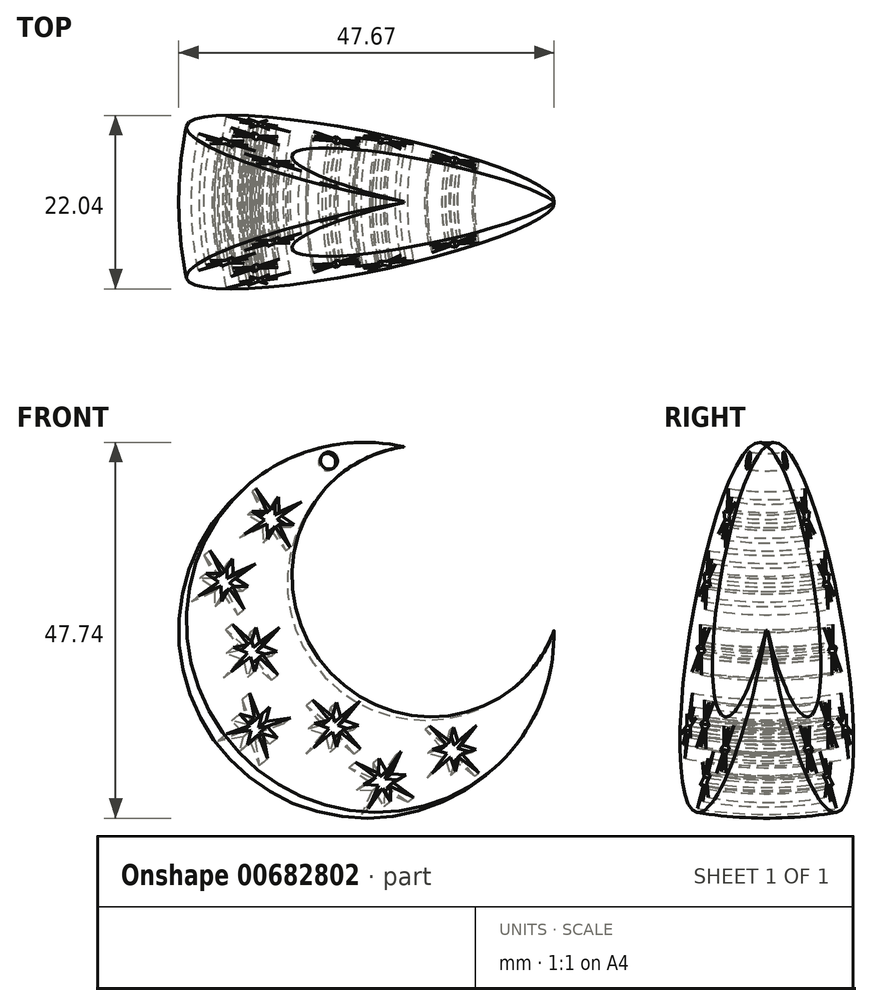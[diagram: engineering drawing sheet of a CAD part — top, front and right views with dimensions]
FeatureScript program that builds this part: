
annotation { "Feature Type Name" : "Feature", "Feature Type Description" : "" }
export const myFeature = defineFeature(function(context is Context, id is Id, definition is map)
    precondition{}
    {
        {
            var Q0;
            Q0=qCreatedBy(makeId("Front.planeOp"),FACE);
            var sketch = newSketch(context, id + "F0", { "sketchPlane" : qUnion([Q0])});
            skArc(sketch, "E0", {"start": v(24.25, 23.35) * mm, "mid": v(1.03, -15.08) * mm, "end": v(43.32, 0) * mm});
            skArc(sketch, "E1", {"start": v(24.25, 23.35) * mm, "mid": v(13.4, -4.97) * mm, "end": v(43.32, 0) * mm});
            skSolve(sketch);
        }
        {
            var Q0;
            Q0=qCreatedBy(makeId("Front.planeOp"),FACE);
            var sketch = newSketch(context, id + "F1", { "sketchPlane" : qUnion([Q0])});
            skLineSegment(sketch, "E2", {"start": v(24.45, 23.46) * mm, "end": v(43.82, 0) * mm});
            skSolve(sketch);
        }
        {
            var Q0;
            Q0 = qSketchRegion(id + "F0", true);
            var Q1;
            Q1 = qConstructionFilter(qBodyType(qCreatedBy(id + "F0" ,EDGE), BodyType.WIRE), ConstructionObject.NO);
            var Q2;
            Q2=sQuery(id+"F1.wireOp",EDGE,"E2");
            revolve(context, id + "F2", {"entities" : qUnion([Q0]), "surfaceEntities" : qUnion([Q1]), "axis" : qUnion([Q2]), "revolveType" : RevolveType.SYMMETRIC, "angle" : 30 * degree});
        }
        {
            var Q0;
            Q0=makeQuery(id+"F2.opRevolve","CAP_FACE",FACE,{"disambiguationData":[OSD([sQuery(id+"F0.wireOp",EDGE,"E0"),sQuery(id+"F0.wireOp",EDGE,"E1")])],"isStart":true});
            var sketch = newSketch(context, id + "F3", { "sketchPlane" : qUnion([Q0])});
            skLineSegment(sketch, "E3", {"start": v(3.8, 17) * mm, "end": v(5.2, 14.07) * mm});
            skLineSegment(sketch, "E4", {"start": v(5.75, 14.37) * mm, "end": v(3.8, 17) * mm});
            skLineSegment(sketch, "E5", {"start": v(8.21, 9.52) * mm, "end": v(6.8, 12.45) * mm});
            skLineSegment(sketch, "E6", {"start": v(6.27, 12.15) * mm, "end": v(8.21, 9.52) * mm});
            skLineSegment(sketch, "E7", {"start": v(9.71, 15.47) * mm, "end": v(6.8, 14.08) * mm});
            skLineSegment(sketch, "E8", {"start": v(7.09, 13.53) * mm, "end": v(9.71, 15.47) * mm});
            skLineSegment(sketch, "E9", {"start": v(2.3, 11.04) * mm, "end": v(5.23, 12.43) * mm});
            skLineSegment(sketch, "E10", {"start": v(4.93, 13) * mm, "end": v(2.3, 11.04) * mm});
            skLineSegment(sketch, "E11", {"start": v(6.75, 16.01) * mm, "end": v(5.75, 14.37) * mm});
            skLineSegment(sketch, "E12", {"start": v(6.8, 14.08) * mm, "end": v(6.75, 16.01) * mm});
            skLineSegment(sketch, "E13", {"start": v(8.74, 12.5) * mm, "end": v(7.09, 13.53) * mm});
            skLineSegment(sketch, "E14", {"start": v(6.8, 12.45) * mm, "end": v(8.74, 12.5) * mm});
            skLineSegment(sketch, "E15", {"start": v(5.28, 10.5) * mm, "end": v(6.27, 12.15) * mm});
            skLineSegment(sketch, "E16", {"start": v(5.23, 12.43) * mm, "end": v(5.28, 10.5) * mm});
            skLineSegment(sketch, "E17", {"start": v(3.28, 14.02) * mm, "end": v(4.93, 13) * mm});
            skLineSegment(sketch, "E18", {"start": v(5.2, 14.07) * mm, "end": v(3.28, 14.02) * mm});
            skLineSegment(sketch, "E19", {"start": v(-2.16, 8.8) * mm, "end": v(-0.75, 5.86) * mm});
            skLineSegment(sketch, "E20", {"start": v(-0.21, 6.17) * mm, "end": v(-2.16, 8.8) * mm});
            skLineSegment(sketch, "E21", {"start": v(2.25, 1.32) * mm, "end": v(0.85, 4.25) * mm});
            skLineSegment(sketch, "E22", {"start": v(0.3, 3.95) * mm, "end": v(2.25, 1.32) * mm});
            skLineSegment(sketch, "E23", {"start": v(3.75, 7.27) * mm, "end": v(0.83, 5.88) * mm});
            skLineSegment(sketch, "E24", {"start": v(1.13, 5.32) * mm, "end": v(3.75, 7.27) * mm});
            skLineSegment(sketch, "E25", {"start": v(-3.66, 2.84) * mm, "end": v(-0.74, 4.23) * mm});
            skLineSegment(sketch, "E26", {"start": v(-1.03, 4.79) * mm, "end": v(-3.66, 2.84) * mm});
            skLineSegment(sketch, "E27", {"start": v(0.78, 7.81) * mm, "end": v(-0.21, 6.17) * mm});
            skLineSegment(sketch, "E28", {"start": v(0.83, 5.88) * mm, "end": v(0.78, 7.81) * mm});
            skLineSegment(sketch, "E29", {"start": v(2.78, 4.3) * mm, "end": v(1.13, 5.32) * mm});
            skLineSegment(sketch, "E30", {"start": v(0.85, 4.25) * mm, "end": v(2.78, 4.3) * mm});
            skLineSegment(sketch, "E31", {"start": v(-0.68, 2.3) * mm, "end": v(0.3, 3.95) * mm});
            skLineSegment(sketch, "E32", {"start": v(-0.74, 4.23) * mm, "end": v(-0.68, 2.3) * mm});
            skLineSegment(sketch, "E33", {"start": v(-2.69, 5.82) * mm, "end": v(-1.03, 4.79) * mm});
            skLineSegment(sketch, "E34", {"start": v(-0.75, 5.86) * mm, "end": v(-2.69, 5.82) * mm});
            skLineSegment(sketch, "E35", {"start": v(0.75, -0.62) * mm, "end": v(2.75, -3.17) * mm});
            skLineSegment(sketch, "E36", {"start": v(3.22, -2.76) * mm, "end": v(0.75, -0.62) * mm});
            skLineSegment(sketch, "E37", {"start": v(6.67, -6.95) * mm, "end": v(4.67, -4.4) * mm});
            skLineSegment(sketch, "E38", {"start": v(4.2, -4.81) * mm, "end": v(6.67, -6.95) * mm});
            skLineSegment(sketch, "E39", {"start": v(6.84, -0.82) * mm, "end": v(4.3, -2.8) * mm});
            skLineSegment(sketch, "E40", {"start": v(4.7, -3.29) * mm, "end": v(6.84, -0.82) * mm});
            skLineSegment(sketch, "E41", {"start": v(0.58, -6.75) * mm, "end": v(3.13, -4.76) * mm});
            skLineSegment(sketch, "E42", {"start": v(2.72, -4.28) * mm, "end": v(0.58, -6.75) * mm});
            skLineSegment(sketch, "E43", {"start": v(3.83, -0.93) * mm, "end": v(3.22, -2.76) * mm});
            skLineSegment(sketch, "E44", {"start": v(4.3, -2.8) * mm, "end": v(3.83, -0.93) * mm});
            skLineSegment(sketch, "E45", {"start": v(6.54, -3.93) * mm, "end": v(4.7, -3.29) * mm});
            skLineSegment(sketch, "E46", {"start": v(4.67, -4.4) * mm, "end": v(6.54, -3.93) * mm});
            skLineSegment(sketch, "E47", {"start": v(3.6, -6.63) * mm, "end": v(4.2, -4.81) * mm});
            skLineSegment(sketch, "E48", {"start": v(3.13, -4.76) * mm, "end": v(3.6, -6.63) * mm});
            skLineSegment(sketch, "E49", {"start": v(0.88, -3.63) * mm, "end": v(2.72, -4.28) * mm});
            skLineSegment(sketch, "E50", {"start": v(2.75, -3.17) * mm, "end": v(0.88, -3.63) * mm});
            skLineSegment(sketch, "E51", {"start": v(2.99, -9.43) * mm, "end": v(3.58, -12.62) * mm});
            skLineSegment(sketch, "E52", {"start": v(4.19, -12.47) * mm, "end": v(2.99, -9.43) * mm});
            skLineSegment(sketch, "E53", {"start": v(5.3, -17.79) * mm, "end": v(4.72, -14.59) * mm});
            skLineSegment(sketch, "E54", {"start": v(4.11, -14.75) * mm, "end": v(5.3, -17.79) * mm});
            skLineSegment(sketch, "E55", {"start": v(8.3, -12.43) * mm, "end": v(5.12, -13.01) * mm});
            skLineSegment(sketch, "E56", {"start": v(5.26, -13.63) * mm, "end": v(8.3, -12.43) * mm});
            skLineSegment(sketch, "E57", {"start": v(0, -14.79) * mm, "end": v(3.18, -14.2) * mm});
            skLineSegment(sketch, "E58", {"start": v(3.04, -13.59) * mm, "end": v(0, -14.79) * mm});
            skLineSegment(sketch, "E59", {"start": v(5.57, -11.14) * mm, "end": v(4.19, -12.47) * mm});
            skLineSegment(sketch, "E60", {"start": v(5.12, -13.01) * mm, "end": v(5.57, -11.14) * mm});
            skLineSegment(sketch, "E61", {"start": v(6.6, -15.04) * mm, "end": v(5.26, -13.63) * mm});
            skLineSegment(sketch, "E62", {"start": v(4.72, -14.59) * mm, "end": v(6.6, -15.04) * mm});
            skLineSegment(sketch, "E63", {"start": v(2.73, -16.08) * mm, "end": v(4.11, -14.75) * mm});
            skLineSegment(sketch, "E64", {"start": v(3.18, -14.2) * mm, "end": v(2.73, -16.08) * mm});
            skLineSegment(sketch, "E65", {"start": v(1.7, -12.16) * mm, "end": v(3.04, -13.59) * mm});
            skLineSegment(sketch, "E66", {"start": v(3.58, -12.62) * mm, "end": v(1.7, -12.16) * mm});
            skLineSegment(sketch, "E67", {"start": v(16.7, -17.87) * mm, "end": v(19.38, -19.7) * mm});
            skLineSegment(sketch, "E68", {"start": v(19.7, -19.18) * mm, "end": v(16.7, -17.87) * mm});
            skLineSegment(sketch, "E69", {"start": v(24.25, -22.14) * mm, "end": v(21.57, -20.3) * mm});
            skLineSegment(sketch, "E70", {"start": v(21.26, -20.84) * mm, "end": v(24.25, -22.14) * mm});
            skLineSegment(sketch, "E71", {"start": v(22.58, -16.24) * mm, "end": v(20.75, -18.9) * mm});
            skLineSegment(sketch, "E72", {"start": v(21.28, -19.24) * mm, "end": v(22.58, -16.24) * mm});
            skLineSegment(sketch, "E73", {"start": v(18.38, -23.78) * mm, "end": v(20.21, -21.11) * mm});
            skLineSegment(sketch, "E74", {"start": v(19.68, -20.78) * mm, "end": v(18.38, -23.78) * mm});
            skLineSegment(sketch, "E75", {"start": v(19.74, -17.25) * mm, "end": v(19.7, -19.18) * mm});
            skLineSegment(sketch, "E76", {"start": v(20.75, -18.9) * mm, "end": v(19.74, -17.25) * mm});
            skLineSegment(sketch, "E77", {"start": v(23.22, -19.3) * mm, "end": v(21.28, -19.24) * mm});
            skLineSegment(sketch, "E78", {"start": v(21.57, -20.3) * mm, "end": v(23.22, -19.3) * mm});
            skLineSegment(sketch, "E79", {"start": v(21.23, -22.76) * mm, "end": v(21.26, -20.84) * mm});
            skLineSegment(sketch, "E80", {"start": v(20.21, -21.11) * mm, "end": v(21.23, -22.76) * mm});
            skLineSegment(sketch, "E81", {"start": v(17.73, -20.71) * mm, "end": v(19.68, -20.78) * mm});
            skLineSegment(sketch, "E82", {"start": v(19.38, -19.7) * mm, "end": v(17.73, -20.71) * mm});
            skLineSegment(sketch, "E83", {"start": v(26.3, -12.87) * mm, "end": v(28.5, -15.24) * mm});
            skLineSegment(sketch, "E84", {"start": v(28.93, -14.79) * mm, "end": v(26.3, -12.87) * mm});
            skLineSegment(sketch, "E85", {"start": v(32.73, -18.68) * mm, "end": v(30.52, -16.3) * mm});
            skLineSegment(sketch, "E86", {"start": v(30.09, -16.75) * mm, "end": v(32.73, -18.68) * mm});
            skLineSegment(sketch, "E87", {"start": v(32.38, -12.55) * mm, "end": v(30.01, -14.75) * mm});
            skLineSegment(sketch, "E88", {"start": v(30.46, -15.2) * mm, "end": v(32.38, -12.55) * mm});
            skLineSegment(sketch, "E89", {"start": v(26.64, -19) * mm, "end": v(29.01, -16.8) * mm});
            skLineSegment(sketch, "E90", {"start": v(28.56, -16.35) * mm, "end": v(26.64, -19) * mm});
            skLineSegment(sketch, "E91", {"start": v(29.39, -12.92) * mm, "end": v(28.93, -14.79) * mm});
            skLineSegment(sketch, "E92", {"start": v(30.01, -14.75) * mm, "end": v(29.39, -12.92) * mm});
            skLineSegment(sketch, "E93", {"start": v(32.34, -15.67) * mm, "end": v(30.46, -15.2) * mm});
            skLineSegment(sketch, "E94", {"start": v(30.52, -16.3) * mm, "end": v(32.34, -15.67) * mm});
            skLineSegment(sketch, "E95", {"start": v(29.64, -18.62) * mm, "end": v(30.09, -16.75) * mm});
            skLineSegment(sketch, "E96", {"start": v(29.01, -16.8) * mm, "end": v(29.64, -18.62) * mm});
            skLineSegment(sketch, "E97", {"start": v(26.68, -15.86) * mm, "end": v(28.56, -16.35) * mm});
            skLineSegment(sketch, "E98", {"start": v(28.5, -15.24) * mm, "end": v(26.68, -15.86) * mm});
            skLineSegment(sketch, "E99", {"start": v(11.16, -10.05) * mm, "end": v(13.27, -12.52) * mm});
            skLineSegment(sketch, "E100", {"start": v(13.71, -12.08) * mm, "end": v(11.16, -10.05) * mm});
            skLineSegment(sketch, "E101", {"start": v(17.34, -16.13) * mm, "end": v(15.23, -13.66) * mm});
            skLineSegment(sketch, "E102", {"start": v(14.79, -14.1) * mm, "end": v(17.34, -16.13) * mm});
            skLineSegment(sketch, "E103", {"start": v(17.26, -10) * mm, "end": v(14.8, -12.1) * mm});
            skLineSegment(sketch, "E104", {"start": v(15.22, -12.55) * mm, "end": v(17.26, -10) * mm});
            skLineSegment(sketch, "E105", {"start": v(11.25, -16.18) * mm, "end": v(13.7, -14.09) * mm});
            skLineSegment(sketch, "E106", {"start": v(13.28, -13.63) * mm, "end": v(11.25, -16.18) * mm});
            skLineSegment(sketch, "E107", {"start": v(14.25, -10.24) * mm, "end": v(13.71, -12.08) * mm});
            skLineSegment(sketch, "E108", {"start": v(14.8, -12.1) * mm, "end": v(14.25, -10.24) * mm});
            skLineSegment(sketch, "E109", {"start": v(17.09, -13.11) * mm, "end": v(15.22, -12.55) * mm});
            skLineSegment(sketch, "E110", {"start": v(15.23, -13.66) * mm, "end": v(17.09, -13.11) * mm});
            skLineSegment(sketch, "E111", {"start": v(14.26, -15.94) * mm, "end": v(14.79, -14.1) * mm});
            skLineSegment(sketch, "E112", {"start": v(13.7, -14.09) * mm, "end": v(14.26, -15.94) * mm});
            skLineSegment(sketch, "E113", {"start": v(11.41, -13.06) * mm, "end": v(13.28, -13.63) * mm});
            skLineSegment(sketch, "E114", {"start": v(13.27, -12.52) * mm, "end": v(11.41, -13.06) * mm});
            skSolve(sketch);
        }
        {
            var Q0;
            Q0=makeQuery(id+"F3.imprint","IMPRINT",FACE,{"disambiguationData":[TD([[makeQuery(id+"F3.imprint","IMPRINT",EDGE,{"derivedFrom":sQuery(id+"F3.wireOp",EDGE,"E3")}),-1.0]])]});
            var sketch = newSketch(context, id + "F4", { "sketchPlane" : qUnion([Q0])});
            skCircle(sketch, "E115", {"center": v(13.26, 20.9) * mm, "radius": 1.1 * mm});
            skSolve(sketch);
        }
        {
            var Q0;
            Q0 = qSketchRegion(id + "F4", true);
            var Q1;
            Q1=sQuery(id+"F1.wireOp",EDGE,"E2");
            revolve(context, id + "F5", {"operationType" : NewBodyOperationType.REMOVE, "entities" : qUnion([Q0]), "axis" : qUnion([Q1]), "revolveType" : RevolveType.FULL, "oppositeDirection" : true});
        }
        {
            var Q0;
            Q0 = qSketchRegion(id + "F3", true);
            var Q1;
            Q1=sQuery(id+"F1.wireOp",EDGE,"E2");
            revolve(context, id + "F6", {"operationType" : NewBodyOperationType.REMOVE, "entities" : qUnion([Q0]), "axis" : qUnion([Q1]), "revolveType" : RevolveType.FULL, "oppositeDirection" : true});
        }
    });
